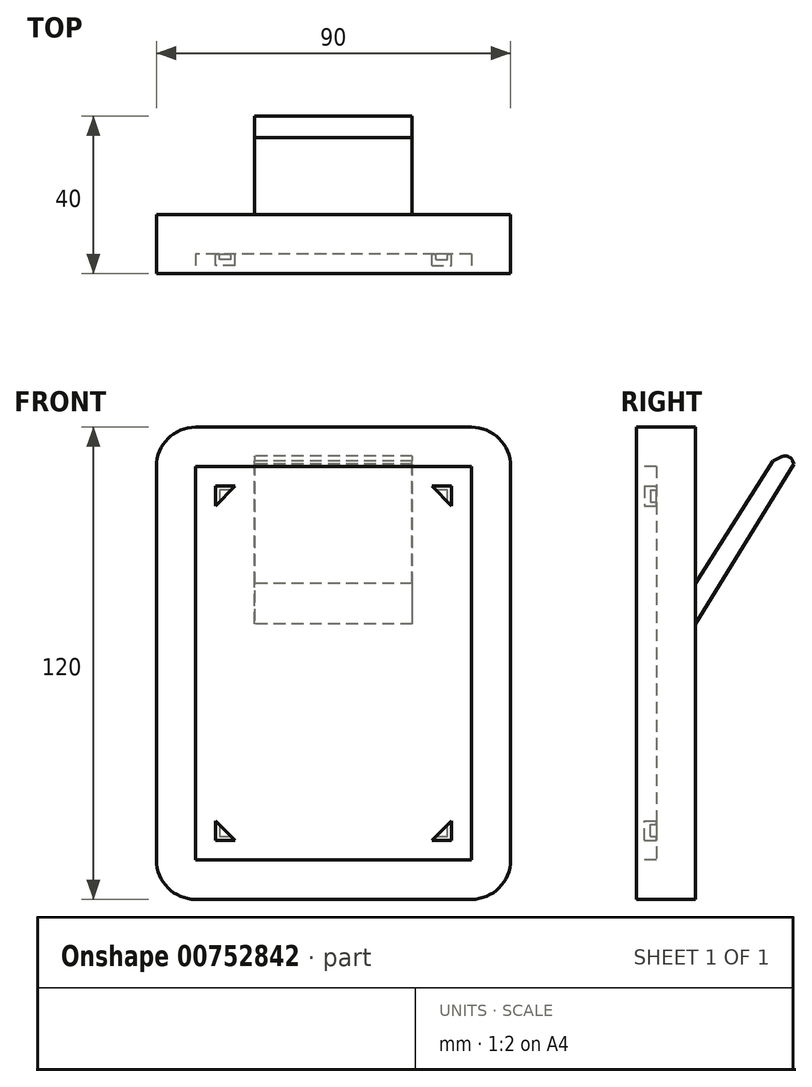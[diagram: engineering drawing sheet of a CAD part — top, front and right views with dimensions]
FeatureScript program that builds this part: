
annotation { "Feature Type Name" : "Feature", "Feature Type Description" : "" }
export const myFeature = defineFeature(function(context is Context, id is Id, definition is map)
    precondition{}
    {
        {
            var Q0;
            Q0=qCreatedBy(makeId("Front.planeOp"),FACE);
            var sketch = newSketch(context, id + "F0", { "sketchPlane" : qUnion([Q0])});
            skLineSegment(sketch, "E0", {"start": v(-90, -10) * mm, "end": v(-90, -110) * mm});
            skLineSegment(sketch, "E1", {"start": v(-80, -120) * mm, "end": v(-10, -120) * mm});
            skLineSegment(sketch, "E2", {"start": v(0, -110) * mm, "end": v(0, -10) * mm});
            skLineSegment(sketch, "E3", {"start": v(-10, 0) * mm, "end": v(-80, 0) * mm});
            skPoint(sketch, "E4.visualSharp", {"position": v(-90, -120) * mm});
            skArc(sketch, "E4.filletArc", {"start": v(-90, -110) * mm, "mid": v(-87.07, -117.07) * mm, "end": v(-80, -120) * mm});
            skPoint(sketch, "E5.visualSharp", {"position": v(0, -120) * mm});
            skArc(sketch, "E5.filletArc", {"start": v(-10, -120) * mm, "mid": v(-2.93, -117.07) * mm, "end": v(0, -110) * mm});
            skPoint(sketch, "E6.visualSharp", {"position": v(0, 0) * mm});
            skArc(sketch, "E6.filletArc", {"start": v(0, -10) * mm, "mid": v(-2.93, -2.93) * mm, "end": v(-10, 0) * mm});
            skPoint(sketch, "E7.visualSharp", {"position": v(-90, 0) * mm});
            skArc(sketch, "E7.filletArc", {"start": v(-80, 0) * mm, "mid": v(-87.07, -2.93) * mm, "end": v(-90, -10) * mm});
            skSolve(sketch);
        }
        {
            var Q0;
            Q0 = qSketchRegion(id + "F0", true);
            extrude(context, id + "F1", {"entities" : qUnion([Q0]), "depth" : 15 * mm, "offsetDistance" : 25 * mm});
        }
        {
            var Q0;
            Q0=makeQuery(id+"F1.opExtrude","CAP_FACE",FACE,{"disambiguationData":[OSD([sQuery(id+"F0.wireOp",EDGE,"E0"),sQuery(id+"F0.wireOp",EDGE,"E1"),sQuery(id+"F0.wireOp",EDGE,"E2"),sQuery(id+"F0.wireOp",EDGE,"E3")])],"isStart":false});
            var sketch = newSketch(context, id + "F2", { "sketchPlane" : qUnion([Q0])});
            skLineSegment(sketch, "E8", {"start": v(-80, -10) * mm, "end": v(-80, -110) * mm});
            skLineSegment(sketch, "E9", {"start": v(-80, -110) * mm, "end": v(-10, -110) * mm});
            skLineSegment(sketch, "E10", {"start": v(-10, -110) * mm, "end": v(-10, -10) * mm});
            skLineSegment(sketch, "E11", {"start": v(-10, -10) * mm, "end": v(-80, -10) * mm});
            skSolve(sketch);
        }
        {
            var Q0;
            Q0 = qSketchRegion(id + "F2", true);
            extrude(context, id + "F3", {"entities" : qUnion([Q0]), "operationType" : NewBodyOperationType.REMOVE, "oppositeDirection" : true, "depth" : 5 * mm, "offsetDistance" : 25 * mm});
        }
        {
            var Q0;
            Q0=makeQuery(id+"F1.opExtrude","CAP_FACE",FACE,{"disambiguationData":[OSD([sQuery(id+"F0.wireOp",EDGE,"E0"),sQuery(id+"F0.wireOp",EDGE,"E1"),sQuery(id+"F0.wireOp",EDGE,"E2"),sQuery(id+"F0.wireOp",EDGE,"E3"),sQuery(id+"F0.wireOp",EDGE,"E4.filletArc"),sQuery(id+"F0.wireOp",EDGE,"E5.filletArc"),sQuery(id+"F0.wireOp",EDGE,"E6.filletArc"),sQuery(id+"F0.wireOp",EDGE,"E7.filletArc")])],"isStart":true});
            var sketch = newSketch(context, id + "F4", { "sketchPlane" : qUnion([Q0])});
            skLineSegment(sketch, "E12", {"start": v(65, -50) * mm, "end": v(65, 0) * mm});
            skLineSegment(sketch, "E13", {"start": v(65, 0) * mm, "end": v(25, 0) * mm});
            skLineSegment(sketch, "E14", {"start": v(25, 0) * mm, "end": v(25, -50) * mm});
            skLineSegment(sketch, "E15", {"start": v(25, -50) * mm, "end": v(65, -50) * mm});
            skSolve(sketch);
        }
        {
            var Q0;
            Q0 = qSketchRegion(id + "F4", true);
            extrude(context, id + "F5", {"entities" : qUnion([Q0]), "operationType" : NewBodyOperationType.ADD, "depth" : 25 * mm, "offsetDistance" : 25 * mm});
        }
        {
            var Q0;
            Q0=makeQuery(id+"F5.opExtrude","SWEPT_FACE",FACE,{"disambiguationData":[OSD([sQuery(id+"F4.wireOp",EDGE,"E12")])]});
            var sketch = newSketch(context, id + "F6", { "sketchPlane" : qUnion([Q0])});
            skLineSegment(sketch, "E16", {"start": v(0, 0) * mm, "end": v(0, -39.7) * mm});
            skLineSegment(sketch, "E17", {"start": v(0, -39.7) * mm, "end": v(-25, 0) * mm});
            skLineSegment(sketch, "E18", {"start": v(-25, 0) * mm, "end": v(0, 0) * mm});
            skLineSegment(sketch, "E19", {"start": v(-25, -50) * mm, "end": v(-25, -9.35) * mm});
            skLineSegment(sketch, "E20", {"start": v(-25, -9.35) * mm, "end": v(0, -50) * mm});
            skLineSegment(sketch, "E21", {"start": v(0, -50) * mm, "end": v(-25, -50) * mm});
            skSolve(sketch);
        }
        {
            var Q0;
            Q0 = qSketchRegion(id + "F6", true);
            extrude(context, id + "F7", {"entities" : qUnion([Q0]), "operationType" : NewBodyOperationType.REMOVE, "oppositeDirection" : true, "depth" : 40 * mm, "offsetDistance" : 25 * mm});
        }
        {
            var Q0;
            Q0=makeQuery(id+"F5.opExtrude","SWEPT_FACE",FACE,{"disambiguationData":[OSD([sQuery(id+"F4.wireOp",EDGE,"E12")])]});
            var sketch = newSketch(context, id + "F8", { "sketchPlane" : qUnion([Q0])});
            skLineSegment(sketch, "E22", {"start": v(-25, 0) * mm, "end": v(-25, -9.35) * mm});
            skLineSegment(sketch, "E23", {"start": v(-25, -9.35) * mm, "end": v(-24.63, -8.52) * mm});
            skLineSegment(sketch, "E24", {"start": v(-21.98, -7.51) * mm, "end": v(-19.6, -8.59) * mm});
            skLineSegment(sketch, "E25", {"start": v(-19.6, -8.59) * mm, "end": v(-25, 0) * mm});
            skPoint(sketch, "E26.visualSharp", {"position": v(-23.8, -6.7) * mm});
            skArc(sketch, "E26.filletArc", {"start": v(-21.98, -7.51) * mm, "mid": v(-23.51, -7.47) * mm, "end": v(-24.63, -8.52) * mm});
            skSolve(sketch);
        }
        {
            var Q0;
            Q0 = qSketchRegion(id + "F8", true);
            extrude(context, id + "F9", {"entities" : qUnion([Q0]), "operationType" : NewBodyOperationType.REMOVE, "oppositeDirection" : true, "depth" : 40 * mm, "offsetDistance" : 25 * mm});
        }
        {
            var Q0;
            Q0=makeQuery(id+"F3.boolean.opBoolean","COPY",FACE,{"derivedFrom":makeQuery(id+"F3.opExtrude","CAP_FACE",FACE,{"disambiguationData":[OSD([sQuery(id+"F2.wireOp",EDGE,"E8"),sQuery(id+"F2.wireOp",EDGE,"E9"),sQuery(id+"F2.wireOp",EDGE,"E10"),sQuery(id+"F2.wireOp",EDGE,"E11")])],"isStart":false})});
            var sketch = newSketch(context, id + "F10", { "sketchPlane" : qUnion([Q0])});
            skLineSegment(sketch, "E27", {"start": v(-15, -20) * mm, "end": v(-15, -15) * mm});
            skLineSegment(sketch, "E28", {"start": v(-15, -15) * mm, "end": v(-20, -15) * mm});
            skLineSegment(sketch, "E29", {"start": v(-20, -15) * mm, "end": v(-15, -20) * mm});
            skLineSegment(sketch, "E30", {"start": v(-75, -100) * mm, "end": v(-75, -105) * mm});
            skLineSegment(sketch, "E31", {"start": v(-75, -105) * mm, "end": v(-70, -105) * mm});
            skLineSegment(sketch, "E32", {"start": v(-70, -105) * mm, "end": v(-75, -100) * mm});
            skLineSegment(sketch, "E33", {"start": v(-70, -15) * mm, "end": v(-75, -15) * mm});
            skLineSegment(sketch, "E34", {"start": v(-75, -15) * mm, "end": v(-75, -20) * mm});
            skLineSegment(sketch, "E35", {"start": v(-75, -20) * mm, "end": v(-70, -15) * mm});
            skLineSegment(sketch, "E36", {"start": v(-20, -105) * mm, "end": v(-15, -105) * mm});
            skLineSegment(sketch, "E37", {"start": v(-15, -105) * mm, "end": v(-15, -100) * mm});
            skLineSegment(sketch, "E38", {"start": v(-15, -100) * mm, "end": v(-20, -105) * mm});
            skSolve(sketch);
        }
        {
            var Q0;
            Q0 = qSketchRegion(id + "F10", true);
            extrude(context, id + "F11", {"entities" : qUnion([Q0]), "operationType" : NewBodyOperationType.ADD, "depth" : 3 * mm, "offsetDistance" : 25 * mm});
        }
        {
            var Q0;
            Q0=makeQuery(id+"F3.boolean.opBoolean","COPY",FACE,{"derivedFrom":makeQuery(id+"F3.opExtrude","CAP_FACE",FACE,{"disambiguationData":[OSD([sQuery(id+"F2.wireOp",EDGE,"E8"),sQuery(id+"F2.wireOp",EDGE,"E9"),sQuery(id+"F2.wireOp",EDGE,"E10"),sQuery(id+"F2.wireOp",EDGE,"E11")])],"isStart":false})});
            var sketch = newSketch(context, id + "F12", { "sketchPlane" : qUnion([Q0])});
            skLineSegment(sketch, "E39", {"start": v(-71, -16) * mm, "end": v(-74, -16) * mm});
            skLineSegment(sketch, "E40", {"start": v(-74, -16) * mm, "end": v(-74, -19) * mm});
            skLineSegment(sketch, "E41", {"start": v(-74, -19) * mm, "end": v(-71, -16) * mm});
            skLineSegment(sketch, "E42", {"start": v(-16, -19) * mm, "end": v(-16, -16) * mm});
            skLineSegment(sketch, "E43", {"start": v(-16, -16) * mm, "end": v(-19, -16) * mm});
            skLineSegment(sketch, "E44", {"start": v(-19, -16) * mm, "end": v(-16, -19) * mm});
            skLineSegment(sketch, "E45", {"start": v(-74, -101) * mm, "end": v(-74, -104) * mm});
            skLineSegment(sketch, "E46", {"start": v(-74, -104) * mm, "end": v(-71, -104) * mm});
            skLineSegment(sketch, "E47", {"start": v(-71, -104) * mm, "end": v(-74, -101) * mm});
            skLineSegment(sketch, "E48", {"start": v(-19, -104) * mm, "end": v(-16, -104) * mm});
            skLineSegment(sketch, "E49", {"start": v(-16, -104) * mm, "end": v(-16, -101) * mm});
            skLineSegment(sketch, "E50", {"start": v(-16, -101) * mm, "end": v(-19, -104) * mm});
            skSolve(sketch);
        }
        {
            var Q0;
            Q0 = qSketchRegion(id + "F12", true);
            extrude(context, id + "F13", {"entities" : qUnion([Q0]), "operationType" : NewBodyOperationType.REMOVE, "depth" : 1.5 * mm, "offsetDistance" : 25 * mm});
        }
        {
            var Q0;
            Q0 = qSketchRegion(id + "F12", true);
            extrude(context, id + "F14", {"entities" : qUnion([Q0]), "operationType" : NewBodyOperationType.REMOVE, "depth" : 1.5 * mm, "offsetDistance" : 25 * mm});
        }
    });
